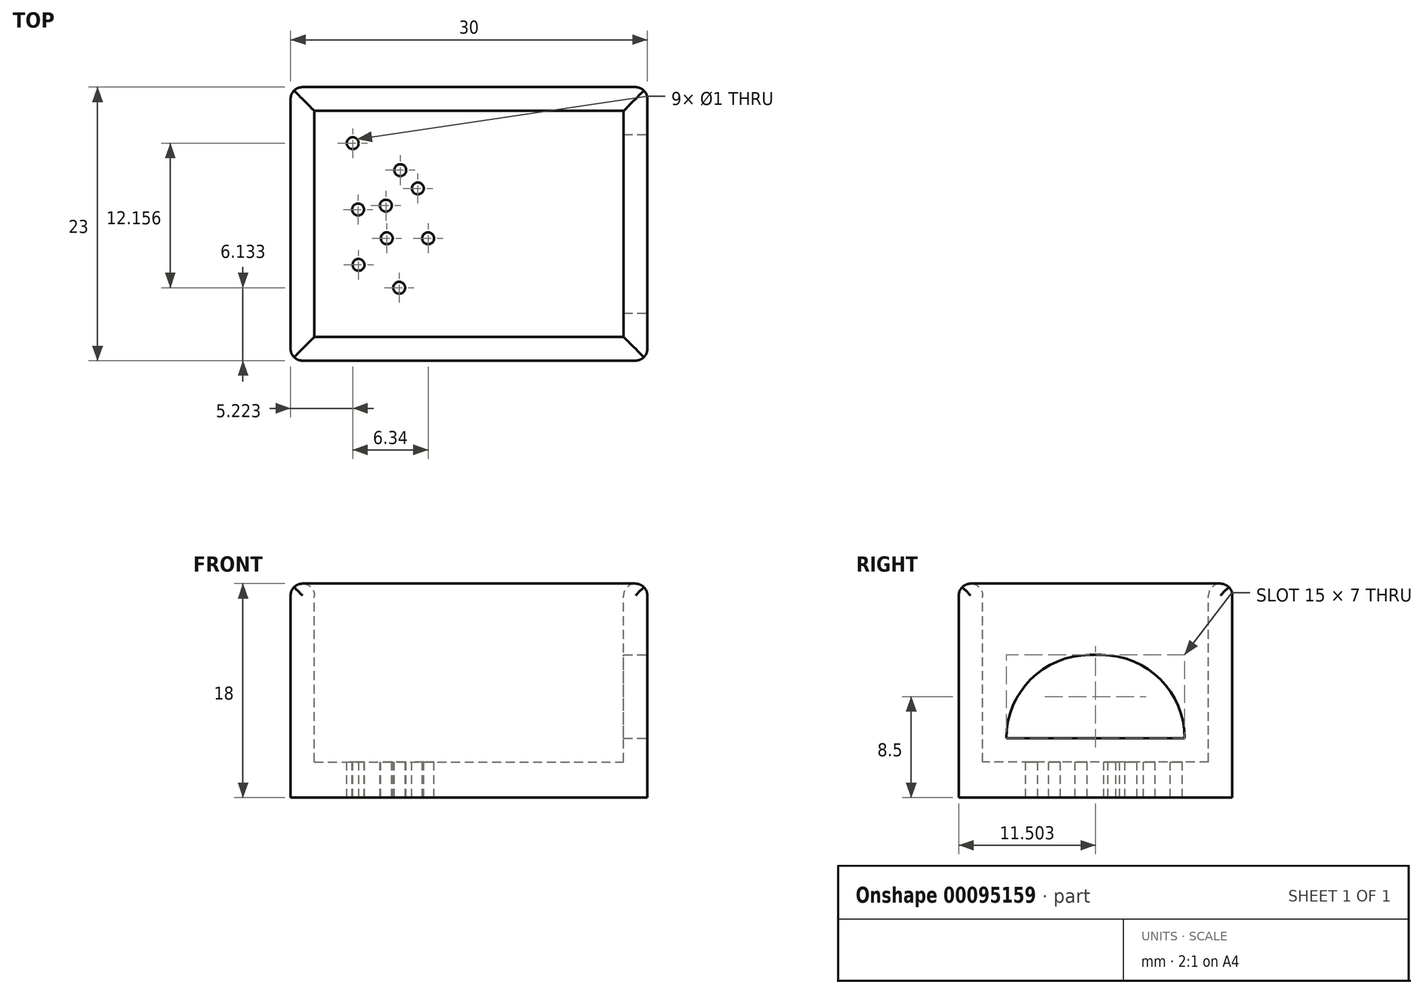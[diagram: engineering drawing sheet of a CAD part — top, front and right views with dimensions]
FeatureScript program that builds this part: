
annotation { "Feature Type Name" : "Feature", "Feature Type Description" : "" }
export const myFeature = defineFeature(function(context is Context, id is Id, definition is map)
    precondition{}
    {
        {
            var Q0;
            Q0=qCreatedBy(makeId("Top.planeOp"),FACE);
            var sketch = newSketch(context, id + "F0", { "sketchPlane" : qUnion([Q0])});
            skLineSegment(sketch, "E0.bottom", {"start": v(-14.11, 12.71) * mm, "end": v(15.89, 12.71) * mm});
            skLineSegment(sketch, "E0.top", {"start": v(-14.11, -10.29) * mm, "end": v(15.89, -10.29) * mm});
            skLineSegment(sketch, "E0.left", {"start": v(-14.11, 12.71) * mm, "end": v(-14.11, -10.29) * mm});
            skLineSegment(sketch, "E0.right", {"start": v(15.89, 12.71) * mm, "end": v(15.89, -10.29) * mm});
            skPoint(sketch, "E1", {"position": v(-9, -6.01) * mm});
            skPoint(sketch, "E2", {"position": v(-9, 9.16) * mm});
            skPoint(sketch, "E3", {"position": v(-8.68, 3.2) * mm});
            skPoint(sketch, "E4", {"position": v(-3.86, -2.75) * mm});
            skPoint(sketch, "E5", {"position": v(-5.34, 4.48) * mm});
            skPoint(sketch, "E6", {"position": v(-1.4, 6.1) * mm});
            skPoint(sketch, "E7", {"position": v(-7.42, -2.98) * mm});
            skPoint(sketch, "E8", {"position": v(-1, -4.5) * mm});
            skPoint(sketch, "E9", {"position": v(-4.86, 8.14) * mm});
            skSolve(sketch);
        }
        {
            var Q0;
            Q0 = qSketchRegion(id + "F0", true);
            extrude(context, id + "F1", {"entities" : qUnion([Q0]), "depth" : 18 * mm});
        }
        {
            var Q0;
            Q0=makeQuery(id+"F1.opExtrude","CAP_FACE",FACE,{"disambiguationData":[OSD([sQuery(id+"F0.wireOp",EDGE,"E0.bottom"),sQuery(id+"F0.wireOp",EDGE,"E0.top"),sQuery(id+"F0.wireOp",EDGE,"E0.left"),sQuery(id+"F0.wireOp",EDGE,"E0.right")])],"isStart":false});
            var sketch = newSketch(context, id + "F2", { "sketchPlane" : qUnion([Q0])});
            skLineSegment(sketch, "E10.bottom", {"start": v(-12.11, 10.71) * mm, "end": v(13.89, 10.71) * mm});
            skLineSegment(sketch, "E10.top", {"start": v(-12.11, -8.29) * mm, "end": v(13.89, -8.29) * mm});
            skLineSegment(sketch, "E10.left", {"start": v(-12.11, 10.71) * mm, "end": v(-12.11, -8.29) * mm});
            skLineSegment(sketch, "E10.right", {"start": v(13.89, 10.71) * mm, "end": v(13.89, -8.29) * mm});
            skSolve(sketch);
        }
        {
            var Q0;
            Q0 = qSketchRegion(id + "F2", true);
            extrude(context, id + "F3", {"entities" : qUnion([Q0]), "operationType" : NewBodyOperationType.REMOVE, "oppositeDirection" : true, "depth" : 15 * mm});
        }
        {
            var Q0;
            Q0=makeQuery(id+"F1.opExtrude","SWEPT_FACE",FACE,{"disambiguationData":[OSD([sQuery(id+"F0.wireOp",EDGE,"E0.right")])]});
            var sketch = newSketch(context, id + "F4", { "sketchPlane" : qUnion([Q0])});
            skLineSegment(sketch, "E11.bottom", {"start": v(1.71, 12) * mm, "end": v(0.71, 12) * mm});
            skLineSegment(sketch, "E11.top", {"start": v(8.71, 5) * mm, "end": v(-6.29, 5) * mm});
            skLineSegment(sketch, "E11.left", {"start": v(8.71, 5) * mm, "end": v(8.71, 5) * mm});
            skLineSegment(sketch, "E11.right", {"start": v(-6.29, 5) * mm, "end": v(-6.29, 5) * mm});
            skPoint(sketch, "E12.visualSharp", {"position": v(-6.29, 12) * mm});
            skArc(sketch, "E12.filletArc", {"start": v(0.71, 12) * mm, "mid": v(-4.24, 9.95) * mm, "end": v(-6.29, 5) * mm});
            skPoint(sketch, "E13.visualSharp", {"position": v(8.71, 12) * mm});
            skArc(sketch, "E13.filletArc", {"start": v(8.71, 5) * mm, "mid": v(6.66, 9.95) * mm, "end": v(1.71, 12) * mm});
            skSolve(sketch);
        }
        {
            var Q0;
            Q0=makeQuery(id+"F4.imprint","IMPRINT",FACE,{"disambiguationData":[TD([[makeQuery(id+"F4.imprint","IMPRINT",EDGE,{"derivedFrom":sQuery(id+"F4.wireOp",EDGE,"E11.bottom")}),1.0]])]});
            extrude(context, id + "F5", {"entities" : qUnion([Q0]), "operationType" : NewBodyOperationType.REMOVE, "oppositeDirection" : true, "depth" : 5 * mm});
        }
        {
            var Q0;
            Q0=makeQuery(id+"F3.boolean.opBoolean","COPY",FACE,{"derivedFrom":makeQuery(id+"F3.opExtrude","CAP_FACE",FACE,{"disambiguationData":[OSD([sQuery(id+"F2.wireOp",EDGE,"E10.bottom"),sQuery(id+"F2.wireOp",EDGE,"E10.top"),sQuery(id+"F2.wireOp",EDGE,"E10.left"),sQuery(id+"F2.wireOp",EDGE,"E10.right")])],"isStart":false})});
            var sketch = newSketch(context, id + "F6", { "sketchPlane" : qUnion([Q0])});
            skPoint(sketch, "E14", {"position": v(-8.4, -2.23) * mm});
            skPoint(sketch, "E15", {"position": v(-8.44, 2.42) * mm});
            skPoint(sketch, "E16", {"position": v(-8.89, 8) * mm});
            skPoint(sketch, "E17", {"position": v(-4.9, 5.73) * mm});
            skPoint(sketch, "E18", {"position": v(-6.02, 0) * mm});
            skPoint(sketch, "E19", {"position": v(-2.55, 0) * mm});
            skPoint(sketch, "E20", {"position": v(-6.1, 2.74) * mm});
            skPoint(sketch, "E21", {"position": v(-3.41, 4.2) * mm});
            skPoint(sketch, "E22", {"position": v(-4.98, -4.16) * mm});
            skSolve(sketch);
        }
        {
            var Q0;
            Q0=sQuery(id+"F6.wireOp",VERTEX,"E19");
            var Q1;
            Q1=sQuery(id+"F6.wireOp",VERTEX,"E21");
            var Q2;
            Q2=sQuery(id+"F6.wireOp",VERTEX,"E17");
            var Q3;
            Q3=sQuery(id+"F6.wireOp",VERTEX,"E20");
            var Q4;
            Q4=sQuery(id+"F6.wireOp",VERTEX,"E18");
            var Q5;
            Q5=sQuery(id+"F6.wireOp",VERTEX,"E14");
            var Q6;
            Q6=sQuery(id+"F6.wireOp",VERTEX,"E15");
            var Q7;
            Q7=sQuery(id+"F6.wireOp",VERTEX,"E16");
            var Q8;
            Q8=sQuery(id+"F6.wireOp",VERTEX,"E22");
            var Q9;
            Q9=makeQuery(id+"F1.opExtrude","SWEPT_BODY",BODY,{"disambiguationData":[OSD([sQuery(id+"F0.wireOp",EDGE,"E0.bottom"),sQuery(id+"F0.wireOp",EDGE,"E0.top"),sQuery(id+"F0.wireOp",EDGE,"E0.left"),sQuery(id+"F0.wireOp",EDGE,"E0.right")])]});
            hole(context, id + "F7", {"style" : HoleStyle.SIMPLE, "endStyle" : HoleEndStyle.THROUGH, "holeDiameter" : 1 * mm, "locations" : qUnion([Q0, Q1, Q2, Q3, Q4, Q5, Q6, Q7, Q8]), "scope" : qUnion([Q9]), "isTappedThrough" : true});
        }
        {
            var Q0;
            Q0=makeQuery(id+"F1.opExtrude","CAP_FACE",FACE,{"disambiguationData":[OSD([sQuery(id+"F0.wireOp",EDGE,"E0.bottom"),sQuery(id+"F0.wireOp",EDGE,"E0.top"),sQuery(id+"F0.wireOp",EDGE,"E0.left"),sQuery(id+"F0.wireOp",EDGE,"E0.right")])],"isStart":false});
            fillet(context, id + "F8", {"entities" : qUnion([Q0]), "radius" : 1 * mm, "tangentPropagation" : true, "allowEdgeOverflow" : false});
        }
        {
            var Q0;
            Q0=makeQuery(id+"F1.opExtrude","SWEPT_EDGE",EDGE,{"disambiguationData":[OSD([sQuery(id+"F0.wireOp",EDGE,"E0.bottom"),sQuery(id+"F0.wireOp",EDGE,"E0.right")])]});
            var Q1;
            Q1=makeQuery(id+"F1.opExtrude","SWEPT_EDGE",EDGE,{"disambiguationData":[OSD([sQuery(id+"F0.wireOp",EDGE,"E0.bottom"),sQuery(id+"F0.wireOp",EDGE,"E0.left")])]});
            var Q2;
            Q2=makeQuery(id+"F1.opExtrude","SWEPT_EDGE",EDGE,{"disambiguationData":[OSD([sQuery(id+"F0.wireOp",EDGE,"E0.top"),sQuery(id+"F0.wireOp",EDGE,"E0.right")])]});
            var Q3;
            Q3=makeQuery(id+"F1.opExtrude","SWEPT_EDGE",EDGE,{"disambiguationData":[OSD([sQuery(id+"F0.wireOp",EDGE,"E0.top"),sQuery(id+"F0.wireOp",EDGE,"E0.left")])]});
            fillet(context, id + "F9", {"entities" : qUnion([Q0, Q1, Q2, Q3]), "radius" : 1 * mm, "tangentPropagation" : true, "allowEdgeOverflow" : false});
        }
    });
